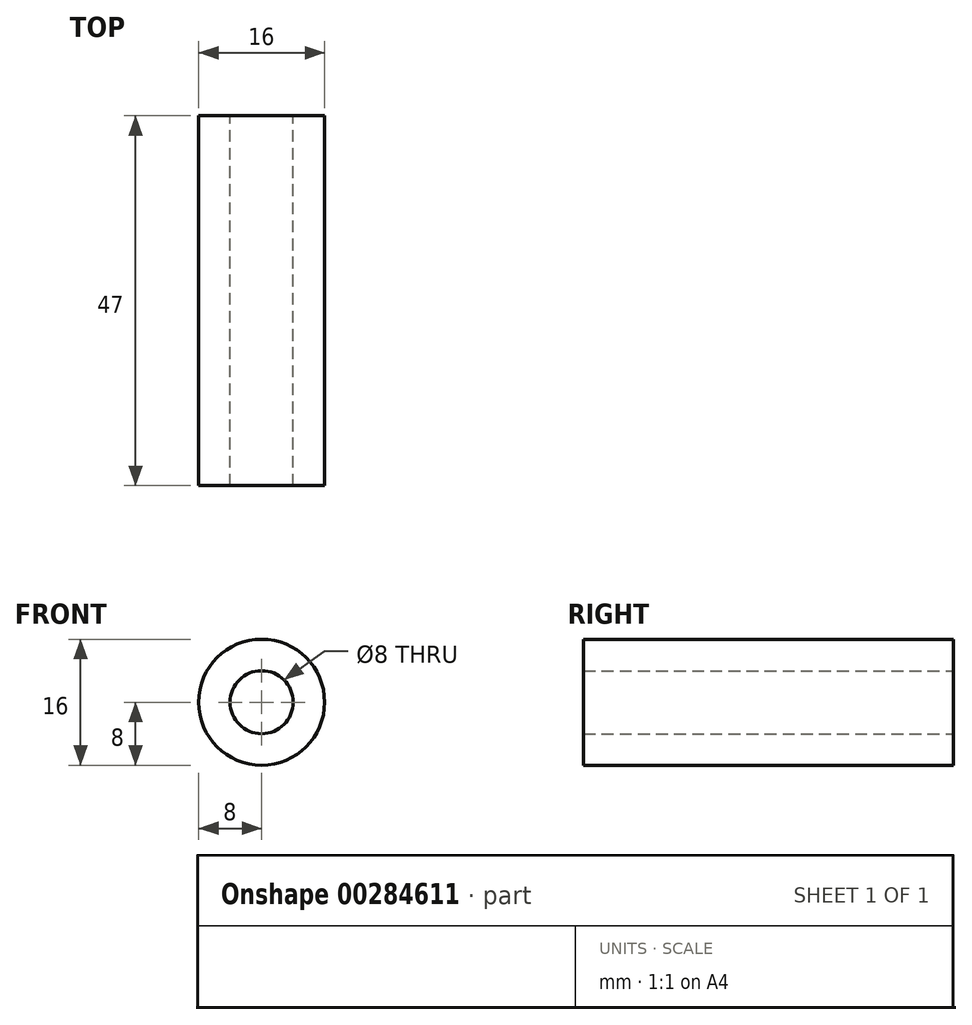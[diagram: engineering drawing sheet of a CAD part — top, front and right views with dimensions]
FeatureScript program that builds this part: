
annotation { "Feature Type Name" : "Feature", "Feature Type Description" : "" }
export const myFeature = defineFeature(function(context is Context, id is Id, definition is map)
    precondition{}
    {
        {
            var Q0;
            Q0=qCreatedBy(makeId("Front.planeOp"),FACE);
            var sketch = newSketch(context, id + "F0", { "sketchPlane" : qUnion([Q0])});
            skCircle(sketch, "E0", {"center": v(0, 0) * mm, "radius": 8 * mm});
            skCircle(sketch, "E1", {"center": v(0, 0) * mm, "radius": 4 * mm});
            skSolve(sketch);
        }
        {
            var Q0;
            Q0 = qSketchRegion(id + "F0", true);
            extrude(context, id + "F1", {"entities" : qUnion([Q0]), "depth" : 47 * mm});
        }
    });
